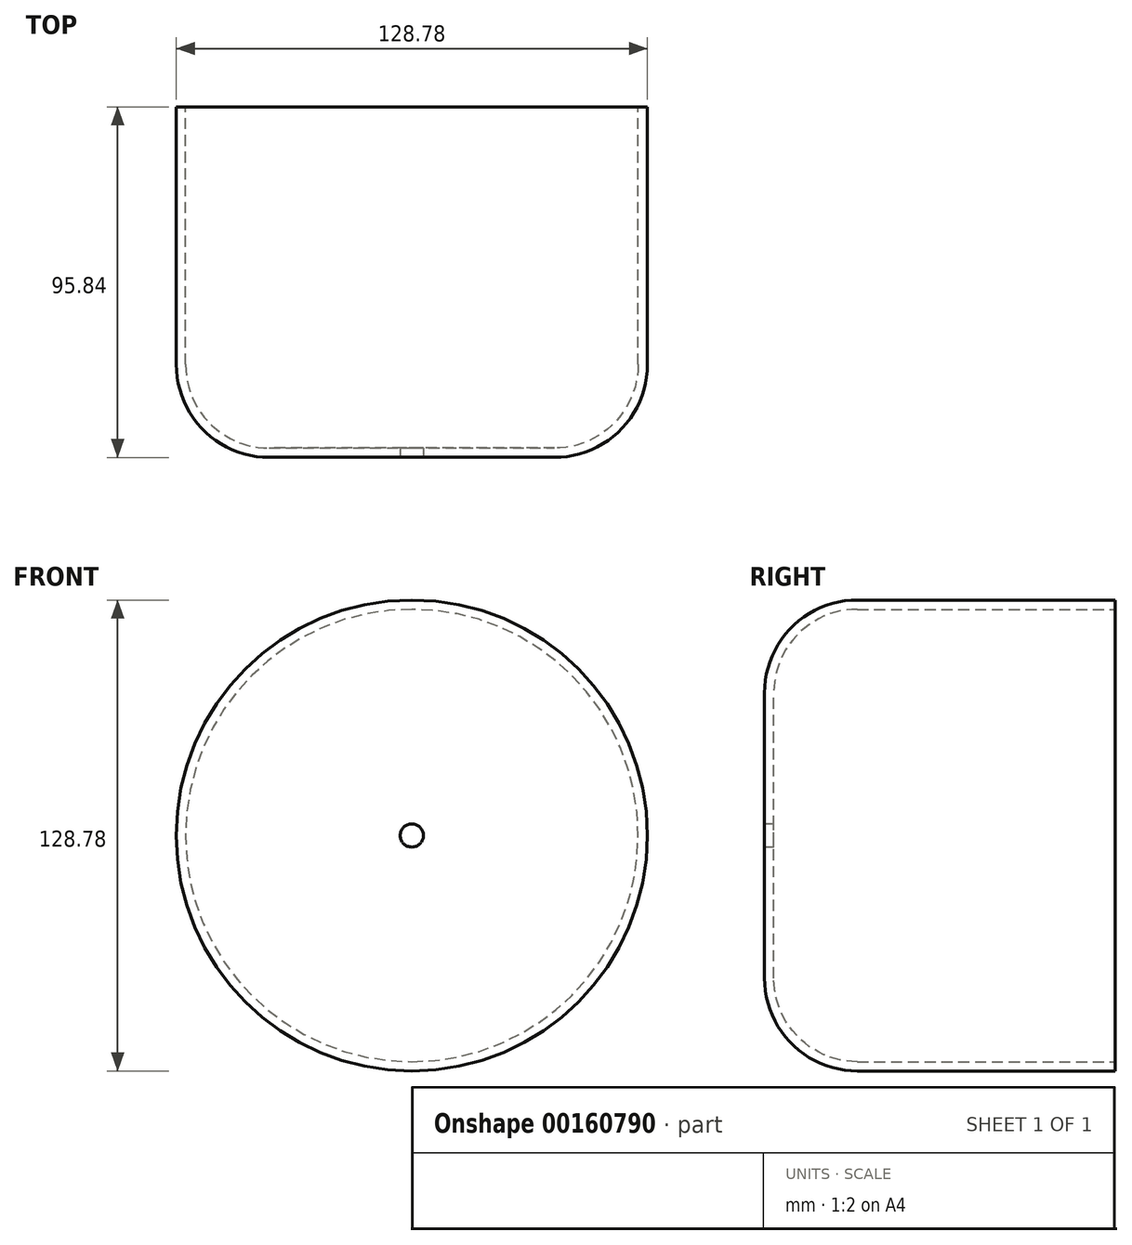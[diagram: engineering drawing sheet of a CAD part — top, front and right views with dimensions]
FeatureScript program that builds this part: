
annotation { "Feature Type Name" : "Feature", "Feature Type Description" : "" }
export const myFeature = defineFeature(function(context is Context, id is Id, definition is map)
    precondition{}
    {
        {
            var Q0;
            Q0=qCreatedBy(makeId("Front.planeOp"),FACE);
            var sketch = newSketch(context, id + "F0", { "sketchPlane" : qUnion([Q0])});
            skCircle(sketch, "E0", {"center": v(0, 0) * mm, "radius": 64.4 * mm});
            skSolve(sketch);
        }
        {
            var Q0;
            Q0 = qSketchRegion(id + "F0", true);
            extrude(context, id + "F1", {"entities" : qUnion([Q0]), "depth" : 95.84 * mm});
        }
        {
            var Q0;
            Q0=makeQuery(id+"F1.opExtrude","CAP_EDGE",EDGE,{"disambiguationData":[OSD([sQuery(id+"F0.wireOp",EDGE,"E0")])],"isStart":false});
            fillet(context, id + "F2", {"entities" : qUnion([Q0]), "radius" : 25.4 * mm, "tangentPropagation" : true, "allowEdgeOverflow" : false});
        }
        {
            var Q0;
            Q0=makeQuery(id+"F1.opExtrude","CAP_FACE",FACE,{"disambiguationData":[OSD([sQuery(id+"F0.wireOp",EDGE,"E0")])],"isStart":true});
            shell(context, id + "F3", {"entities" : qUnion([Q0]), "thickness" : 2.54 * mm});
        }
        {
            var Q0;
            Q0=makeQuery(id+"F1.opExtrude","CAP_FACE",FACE,{"disambiguationData":[OSD([sQuery(id+"F0.wireOp",EDGE,"E0")])],"isStart":false});
            var sketch = newSketch(context, id + "F4", { "sketchPlane" : qUnion([Q0])});
            skPoint(sketch, "E1", {"position": v(0, 0) * mm});
            skSolve(sketch);
        }
        {
            var Q0;
            Q0=sQuery(id+"F4.wireOp",VERTEX,"E1");
            var Q1;
            Q1=makeQuery(id+"F1.opExtrude","SWEPT_BODY",BODY,{"disambiguationData":[OSD([sQuery(id+"F0.wireOp",EDGE,"E0")])]});
            hole(context, id + "F5", {"style" : HoleStyle.SIMPLE, "endStyle" : HoleEndStyle.THROUGH, "holeDiameter" : 6.35 * mm, "locations" : qUnion([Q0]), "scope" : qUnion([Q1]), "isTappedThrough" : true});
        }
    });
